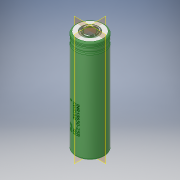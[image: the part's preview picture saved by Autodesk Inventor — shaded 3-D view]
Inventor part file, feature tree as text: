
AUTODESK INVENTOR PART (.ipt)
format: ipt  version: 2019.4 (Build 234330000, 330)  size: 1,010,688 bytes
history: native  units: mm
features: fillet x3, sketch x3, revolve x2, plane x1, emboss x1, chamfer x1
ambient origin geometry x8: Origin, YZ Plane, XZ Plane, XY Plane, X Axis, Y Axis, Z Axis, Center Point
bodies: Solid1 (feature_tree)
feature tree (11):
  revolve  "Revolution1"  [1 undecoded]
  fillet  "Fillet1"  [1 undecoded]
  plane  "Work Plane1"
  emboss  "Emboss2"
  revolve  "Revolution2"  [1 undecoded]
  chamfer  "Chamfer1"  Distance=20.0mm
  fillet  "Fillet4"  Radius=0.01mm
  fillet  "Fillet5"  Radius=3.5mm
  sketch  "Sketch1"  dims[d0=65.0mm d1=9.165mm d2=90.0deg]
  sketch  "Sketch4"  dims[d3=1.0mm d18=0.5mm]
  sketch  "Sketch6"  dims[d19=7.0mm d20=20.0mm d21=0.01mm d22=0.174533mm d23=3.5mm d27=0.7mm d28=2.5mm d29=0.0mm d30=6.0mm d31=90.0deg d32=0.4mm d33=0.4mm d34=0.5mm d35=45.0deg d36=1.0mm d37=2.0mm d38=2.0mm d39=10.0mm d40=0.0mm]
note: 3 required parameter values undecoded (feature->parameter linkage not recoverable at this tier; creation-order binding heuristic only, values carry confidence <= 0.55)